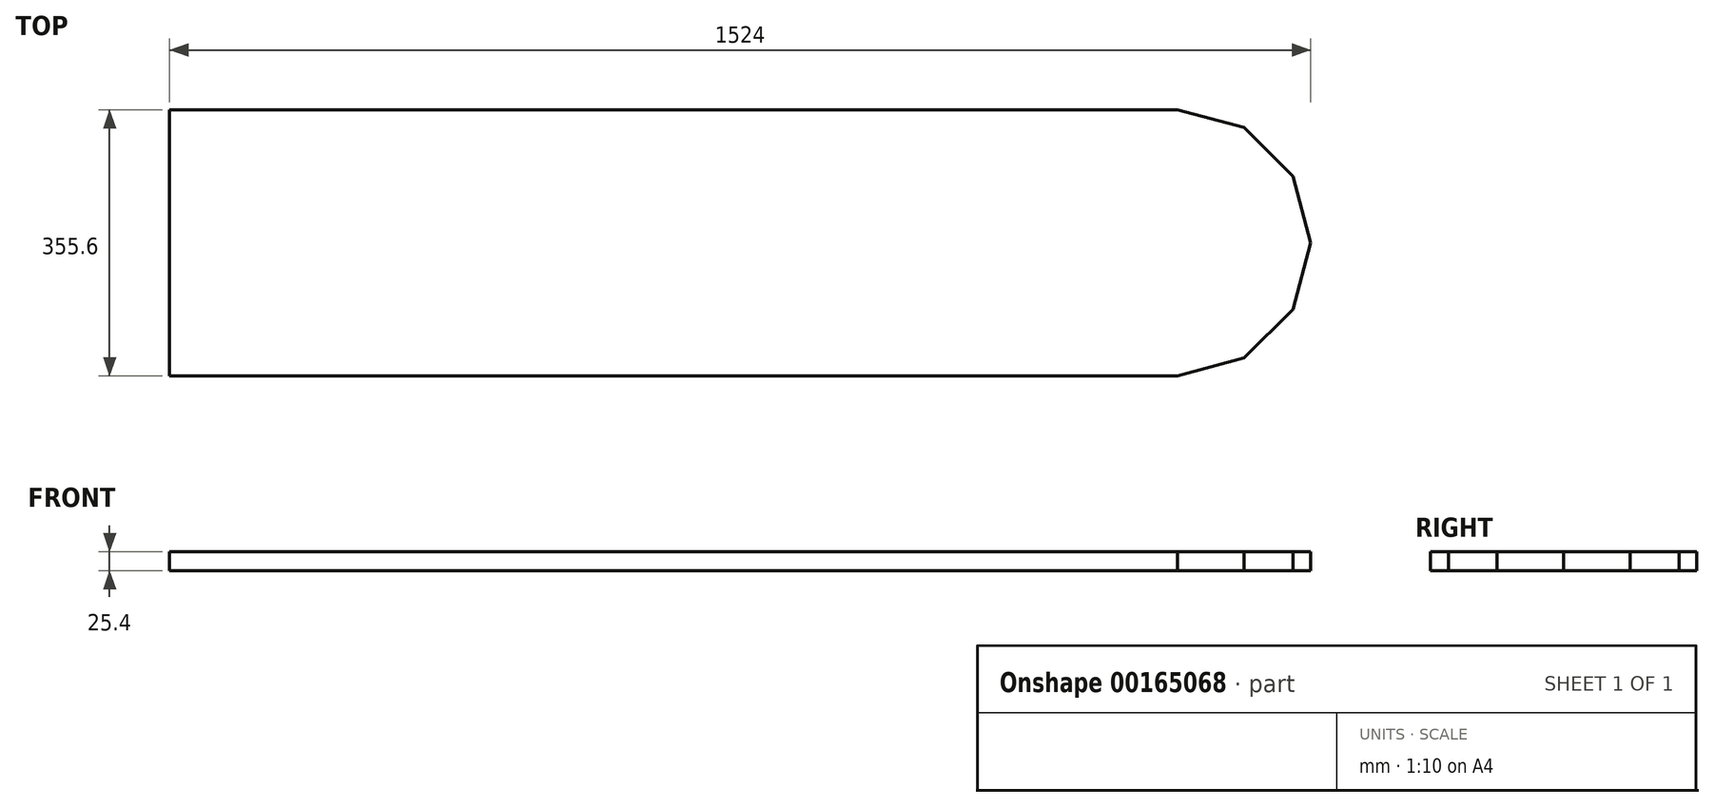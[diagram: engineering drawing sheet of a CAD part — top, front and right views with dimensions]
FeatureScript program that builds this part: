
annotation { "Feature Type Name" : "Feature", "Feature Type Description" : "" }
export const myFeature = defineFeature(function(context is Context, id is Id, definition is map)
    precondition{}
    {
        {
            var Q0;
            Q0=qCreatedBy(makeId("Top.planeOp"),FACE);
            var sketch = newSketch(context, id + "F0", { "sketchPlane" : qUnion([Q0])});
            skLineSegment(sketch, "E0", {"start": v(0, 0) * mm, "end": v(0, -177.8) * mm, "construction": true});
            skLineSegment(sketch, "E1", {"start": v(0, 0) * mm, "end": v(88.9, -153.98) * mm, "construction": true});
            skLineSegment(sketch, "E2", {"start": v(0, 0) * mm, "end": v(153.98, -88.9) * mm, "construction": true});
            skLineSegment(sketch, "E3", {"start": v(0, 0) * mm, "end": v(177.8, 0) * mm, "construction": true});
            skLineSegment(sketch, "E4", {"start": v(0, 0) * mm, "end": v(0, 177.8) * mm, "construction": true});
            skLineSegment(sketch, "E5", {"start": v(0, 0) * mm, "end": v(88.9, 153.98) * mm, "construction": true});
            skLineSegment(sketch, "E6", {"start": v(0, 0) * mm, "end": v(153.98, 88.9) * mm, "construction": true});
            skLineSegment(sketch, "E7", {"start": v(0, 177.8) * mm, "end": v(88.9, 153.98) * mm});
            skLineSegment(sketch, "E8", {"start": v(88.9, 153.98) * mm, "end": v(153.98, 88.9) * mm});
            skLineSegment(sketch, "E9", {"start": v(153.98, 88.9) * mm, "end": v(177.8, 0) * mm});
            skLineSegment(sketch, "E10", {"start": v(177.8, 0) * mm, "end": v(153.98, -88.9) * mm});
            skLineSegment(sketch, "E11", {"start": v(153.98, -88.9) * mm, "end": v(88.9, -153.98) * mm});
            skLineSegment(sketch, "E12", {"start": v(88.9, -153.98) * mm, "end": v(0, -177.8) * mm});
            skLineSegment(sketch, "E13", {"start": v(0, 177.8) * mm, "end": v(-1346.2, 177.8) * mm});
            skLineSegment(sketch, "E14", {"start": v(-1346.2, 177.8) * mm, "end": v(-1346.2, -177.8) * mm});
            skLineSegment(sketch, "E15", {"start": v(-1346.2, -177.8) * mm, "end": v(0, -177.8) * mm});
            skSolve(sketch);
        }
        {
            var Q0;
            Q0=makeQuery(id+"F0.imprint","IMPRINT",FACE,{"disambiguationData":[TD([[makeQuery(id+"F0.imprint","IMPRINT",EDGE,{"derivedFrom":sQuery(id+"F0.wireOp",EDGE,"E7")}),-1.0]])]});
            extrude(context, id + "F1", {"entities" : qUnion([Q0]), "depth" : 25.4 * mm});
        }
    });
